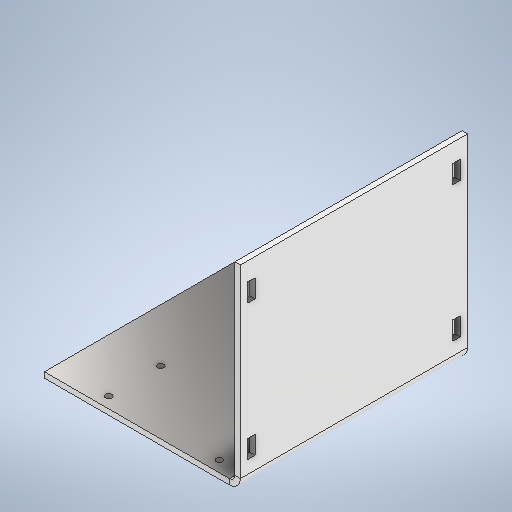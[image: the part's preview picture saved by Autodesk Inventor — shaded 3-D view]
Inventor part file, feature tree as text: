
AUTODESK INVENTOR PART (.ipt)
format: ipt  version: 2025 (Build 290162000, 162)  size: 304,640 bytes
history: native  units: in
note: dims shown in document units (in); Inventor stores cm internally (conversion verified against a paired STEP export)
features: sketch x7, sheet_metal_op x4, other x3, extrude x1
ambient origin geometry x8: Origin, YZ Plane, XZ Plane, XY Plane, X Axis, Y Axis, Z Axis, Center Point
bodies: Solid1 (feature_tree)
feature tree (15):
  sheet_metal_op  "Face1"
  sheet_metal_op  "Flange1"
  extrude  "Extrusion1"  Depth=4.8819in
  sketch  "Sketch1"  dims[d0=4.2126in d1=4.8819in]
  other  "Plate1"
  sketch  "Sketch2"  dims[d24=0.1181in]
  other  "Plate2"
  sheet_metal_op  "Bend1"
  sheet_metal_op  "Corner1"
  sketch  "Sketch6"  dims[d26=0.0591in]
  sketch  "Sketch Rectangular Pattern4"  dims[d25=0.1181in]
  sketch  "Sketch7"  dims[d28=0.1181in]
  sketch  "Sketch Rectangular Pattern6"  dims[d27=0.2362in]
  sketch  "Sketch Rectangular Pattern7"  dims[d29=4.2126in d30=90.0deg d31=0.1181in d32=0.4724in d33=0.1181in d34=0.1181in d79=0.1378in d80=1.1417in d81=0.2362in d82=0.7874in d84=3.2874in d85=0.7874in d87=2.3819in d90=0.1181in d91=0.0in d92=0.3937in d93=0.1575in d94=0.1575in d95=0.5118in d103=0.7874in d105=2.9134in d106=0.7874in d108=4.4094in d111=0.1181in d112=0.0in d113=0.1378in d114=0.2362in d115=1.1417in d116=0.7874in d118=3.2874in d119=0.7874in d121=2.3819in]
  other  "Cut4"
